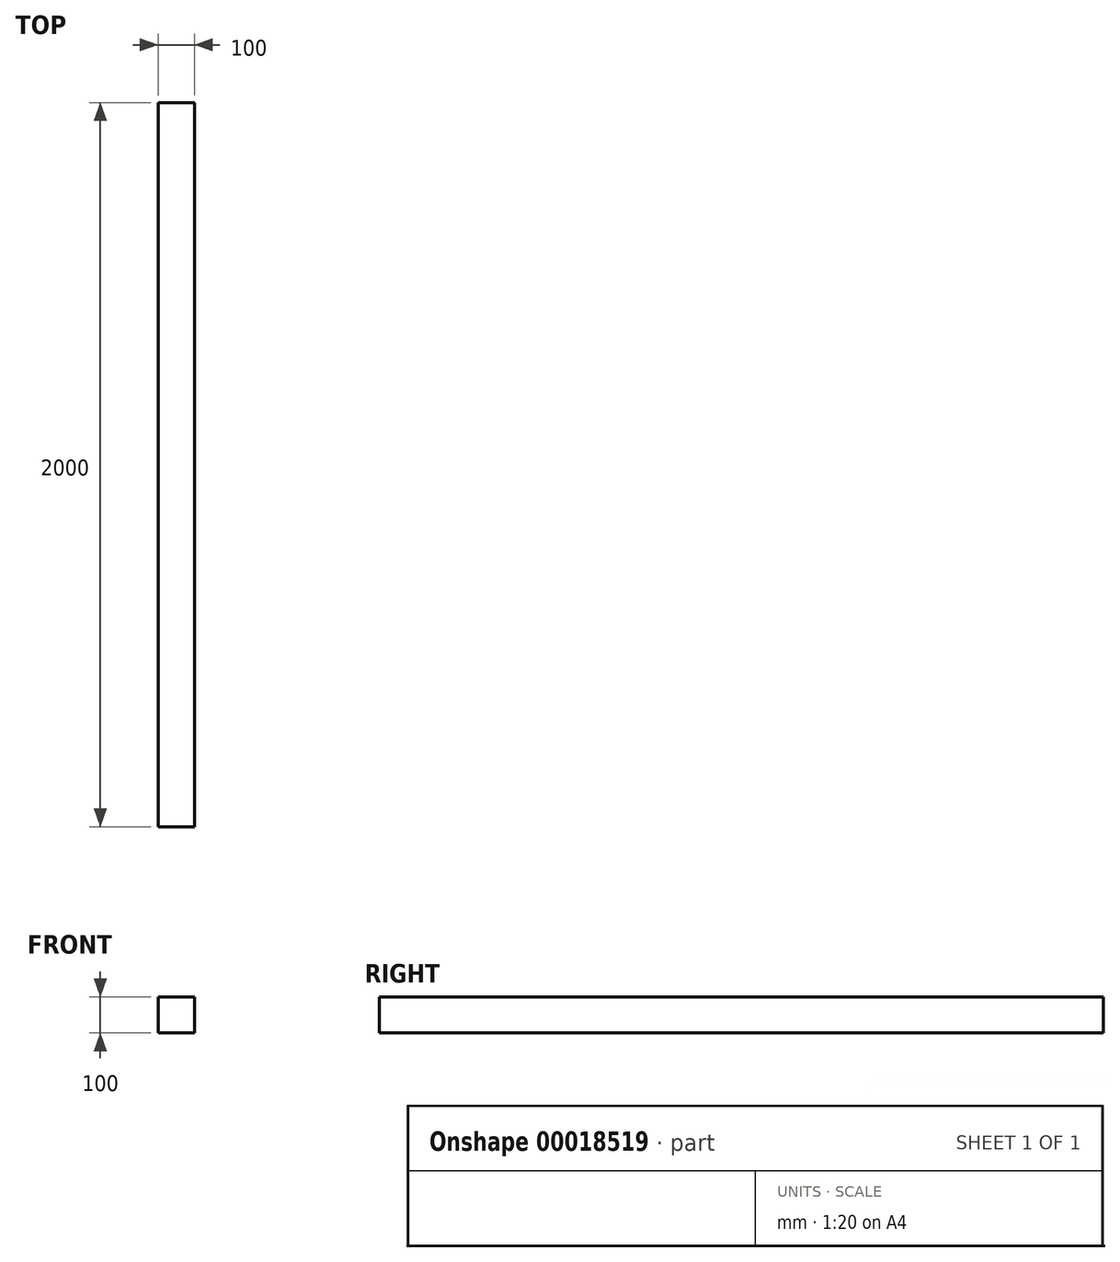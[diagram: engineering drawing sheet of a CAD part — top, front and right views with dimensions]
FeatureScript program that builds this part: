
annotation { "Feature Type Name" : "Feature", "Feature Type Description" : "" }
export const myFeature = defineFeature(function(context is Context, id is Id, definition is map)
    precondition{}
    {
        {
            var Q0;
            Q0=qCreatedBy(makeId("Front.planeOp"),FACE);
            var sketch = newSketch(context, id + "F0", { "sketchPlane" : qUnion([Q0])});
            skLineSegment(sketch, "E0", {"start": v(0, 0) * mm, "end": v(0, 100) * mm});
            skLineSegment(sketch, "E1", {"start": v(0, 100) * mm, "end": v(100, 100) * mm});
            skLineSegment(sketch, "E2", {"start": v(100, 100) * mm, "end": v(100, 0) * mm});
            skLineSegment(sketch, "E3", {"start": v(100, 0) * mm, "end": v(0, 0) * mm});
            skLineSegment(sketch, "E4", {"start": v(50, 100) * mm, "end": v(50, 0) * mm, "construction": true});
            skLineSegment(sketch, "E5", {"start": v(0, 50) * mm, "end": v(100, 50) * mm, "construction": true});
            skPoint(sketch, "E6", {"position": v(50, 50) * mm});
            skSolve(sketch);
        }
        {
            var Q0;
            Q0=makeQuery(id+"F0.imprint","IMPRINT",FACE,{"disambiguationData":[TD([[makeQuery(id+"F0.imprint","IMPRINT",EDGE,{"derivedFrom":sQuery(id+"F0.wireOp",EDGE,"E0")}),-1.0]])]});
            extrude(context, id + "F1", {"entities" : qUnion([Q0]), "depth" : 2000 * mm});
        }
    });
